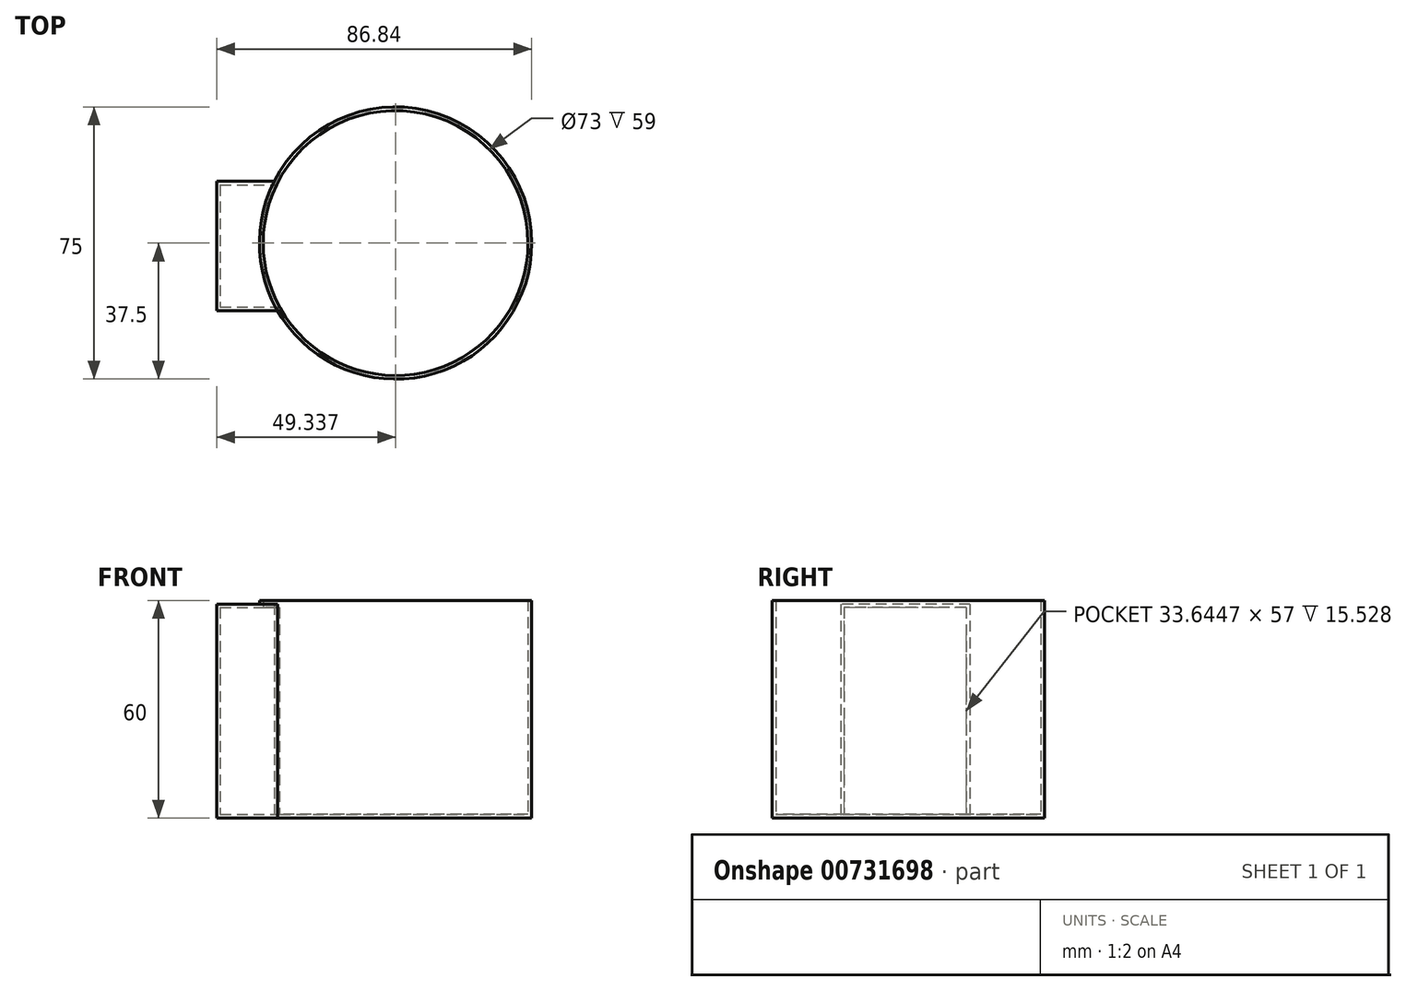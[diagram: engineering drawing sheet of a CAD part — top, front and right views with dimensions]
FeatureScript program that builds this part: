
annotation { "Feature Type Name" : "Feature", "Feature Type Description" : "" }
export const myFeature = defineFeature(function(context is Context, id is Id, definition is map)
    precondition{}
    {
        {
            var Q0;
            Q0=qCreatedBy(makeId("Top.planeOp"),FACE);
            var sketch = newSketch(context, id + "F0", { "sketchPlane" : qUnion([Q0])});
            skCircle(sketch, "E0", {"center": v(49.34, 0) * mm, "radius": 37.5 * mm});
            skSolve(sketch);
        }
        {
            var Q0;
            Q0 = qSketchRegion(id + "F0", true);
            extrude(context, id + "F1", {"entities" : qUnion([Q0]), "depth" : 60 * mm, "offsetDistance" : 25 * mm});
        }
        {
            var Q0;
            Q0=qCreatedBy(makeId("Top.planeOp"),FACE);
            var sketch = newSketch(context, id + "F2", { "sketchPlane" : qUnion([Q0])});
            skLineSegment(sketch, "E1.bottom", {"start": v(0, 17) * mm, "end": v(24.85, 17) * mm});
            skLineSegment(sketch, "E1.top", {"start": v(0, -18.65) * mm, "end": v(24.85, -18.65) * mm});
            skLineSegment(sketch, "E1.left", {"start": v(0, 17) * mm, "end": v(0, -18.65) * mm});
            skLineSegment(sketch, "E1.right", {"start": v(24.85, 17) * mm, "end": v(24.85, -18.65) * mm});
            skSolve(sketch);
        }
        {
            var Q0;
            Q0 = qSketchRegion(id + "F2", true);
            extrude(context, id + "F3", {"entities" : qUnion([Q0]), "operationType" : NewBodyOperationType.ADD, "depth" : 59 * mm, "offsetDistance" : 25 * mm});
        }
        {
            var Q0;
            Q0=makeQuery(id+"F1.opExtrude","CAP_FACE",FACE,{"disambiguationData":[OSD([sQuery(id+"F0.wireOp",EDGE,"E0")])],"isStart":false});
            shell(context, id + "F4", {"entities" : qUnion([Q0]), "thickness" : 1 * mm});
        }
    });
